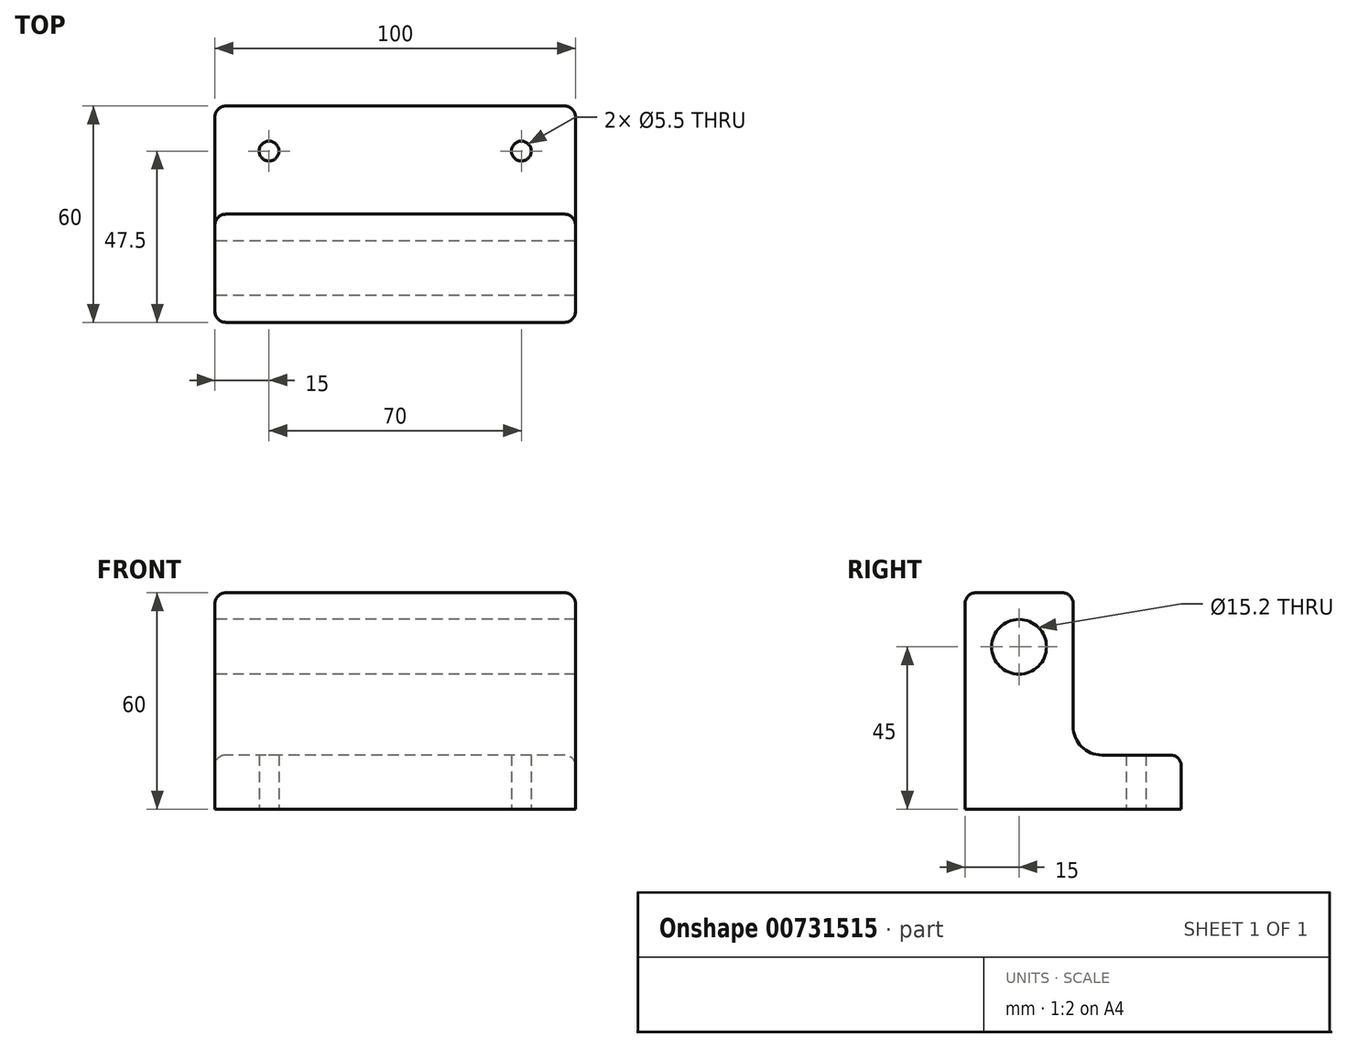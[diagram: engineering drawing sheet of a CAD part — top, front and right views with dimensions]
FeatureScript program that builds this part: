
annotation { "Feature Type Name" : "Feature", "Feature Type Description" : "" }
export const myFeature = defineFeature(function(context is Context, id is Id, definition is map)
    precondition{}
    {
        {
            var Q0;
            Q0=qCreatedBy(makeId("Right.planeOp"),FACE);
            var sketch = newSketch(context, id + "F0", { "sketchPlane" : qUnion([Q0])});
            skLineSegment(sketch, "E0", {"start": v(0, 0) * mm, "end": v(0, 60) * mm});
            skLineSegment(sketch, "E1", {"start": v(0, 60) * mm, "end": v(30, 60) * mm});
            skLineSegment(sketch, "E2", {"start": v(30, 60) * mm, "end": v(30, 23) * mm});
            skLineSegment(sketch, "E3", {"start": v(38, 15) * mm, "end": v(60, 15) * mm});
            skLineSegment(sketch, "E4", {"start": v(60, 15) * mm, "end": v(60, 0) * mm});
            skLineSegment(sketch, "E5", {"start": v(60, 0) * mm, "end": v(0, 0) * mm});
            skCircle(sketch, "E6", {"center": v(15, 45) * mm, "radius": 7.6 * mm});
            skPoint(sketch, "E7.visualSharp", {"position": v(30, 15) * mm});
            skArc(sketch, "E7.filletArc", {"start": v(30, 23) * mm, "mid": v(32.34, 17.34) * mm, "end": v(38, 15) * mm});
            skSolve(sketch);
        }
        {
            var Q0;
            Q0 = qSketchRegion(id + "F0", true);
            extrude(context, id + "F1", {"entities" : qUnion([Q0]), "depth" : 100 * mm, "offsetDistance" : 25 * mm});
        }
        {
            var Q0;
            Q0=qCreatedBy(makeId("Top.planeOp"),FACE);
            var sketch = newSketch(context, id + "F2", { "sketchPlane" : qUnion([Q0])});
            skCircle(sketch, "E8", {"center": v(15, 47.5) * mm, "radius": 2.75 * mm});
            skCircle(sketch, "E9", {"center": v(85, 47.5) * mm, "radius": 2.75 * mm});
            skSolve(sketch);
        }
        {
            var Q0;
            Q0 = qSketchRegion(id + "F2", true);
            extrude(context, id + "F3", {"entities" : qUnion([Q0]), "operationType" : NewBodyOperationType.REMOVE, "depth" : 15 * mm, "offsetDistance" : 25 * mm});
        }
        {
            var Q0;
            Q0=makeQuery(id+"F1.opExtrude","CAP_EDGE",EDGE,{"disambiguationData":[OSD([sQuery(id+"F0.wireOp",EDGE,"E1")])],"isStart":false});
            var Q1;
            Q1=makeQuery(id+"F1.opExtrude","CAP_EDGE",EDGE,{"disambiguationData":[OSD([sQuery(id+"F0.wireOp",EDGE,"E1")])],"isStart":true});
            var Q2;
            Q2=makeQuery(id+"F1.opExtrude","SWEPT_EDGE",EDGE,{"disambiguationData":[OSD([sQuery(id+"F0.wireOp",EDGE,"E1"),sQuery(id+"F0.wireOp",EDGE,"E2")])]});
            var Q3;
            Q3=makeQuery(id+"F1.opExtrude","SWEPT_EDGE",EDGE,{"disambiguationData":[OSD([sQuery(id+"F0.wireOp",EDGE,"E0"),sQuery(id+"F0.wireOp",EDGE,"E1")])]});
            var Q4;
            Q4=makeQuery(id+"F1.opExtrude","CAP_EDGE",EDGE,{"disambiguationData":[OSD([sQuery(id+"F0.wireOp",EDGE,"E3")])],"isStart":false});
            var Q5;
            Q5=makeQuery(id+"F1.opExtrude","SWEPT_EDGE",EDGE,{"disambiguationData":[OSD([sQuery(id+"F0.wireOp",EDGE,"E3"),sQuery(id+"F0.wireOp",EDGE,"E4")])]});
            var Q6;
            Q6=makeQuery(id+"F1.opExtrude","CAP_EDGE",EDGE,{"disambiguationData":[OSD([sQuery(id+"F0.wireOp",EDGE,"E3")])],"isStart":true});
            var Q7;
            Q7=makeQuery(id+"F1.opExtrude","CAP_EDGE",EDGE,{"disambiguationData":[OSD([sQuery(id+"F0.wireOp",EDGE,"E0")])],"isStart":false});
            var Q8;
            Q8=makeQuery(id+"F1.opExtrude","CAP_EDGE",EDGE,{"disambiguationData":[OSD([sQuery(id+"F0.wireOp",EDGE,"E0")])],"isStart":true});
            var Q9;
            Q9=makeQuery(id+"F1.opExtrude","CAP_EDGE",EDGE,{"disambiguationData":[OSD([sQuery(id+"F0.wireOp",EDGE,"E4")])],"isStart":true});
            var Q10;
            Q10=makeQuery(id+"F1.opExtrude","CAP_EDGE",EDGE,{"disambiguationData":[OSD([sQuery(id+"F0.wireOp",EDGE,"E4")])],"isStart":false});
            fillet(context, id + "F4", {"entities" : qUnion([Q0, Q1, Q2, Q3, Q4, Q5, Q6, Q7, Q8, Q9, Q10]), "radius" : 3 * mm, "tangentPropagation" : true, "allowEdgeOverflow" : false});
        }
    });
